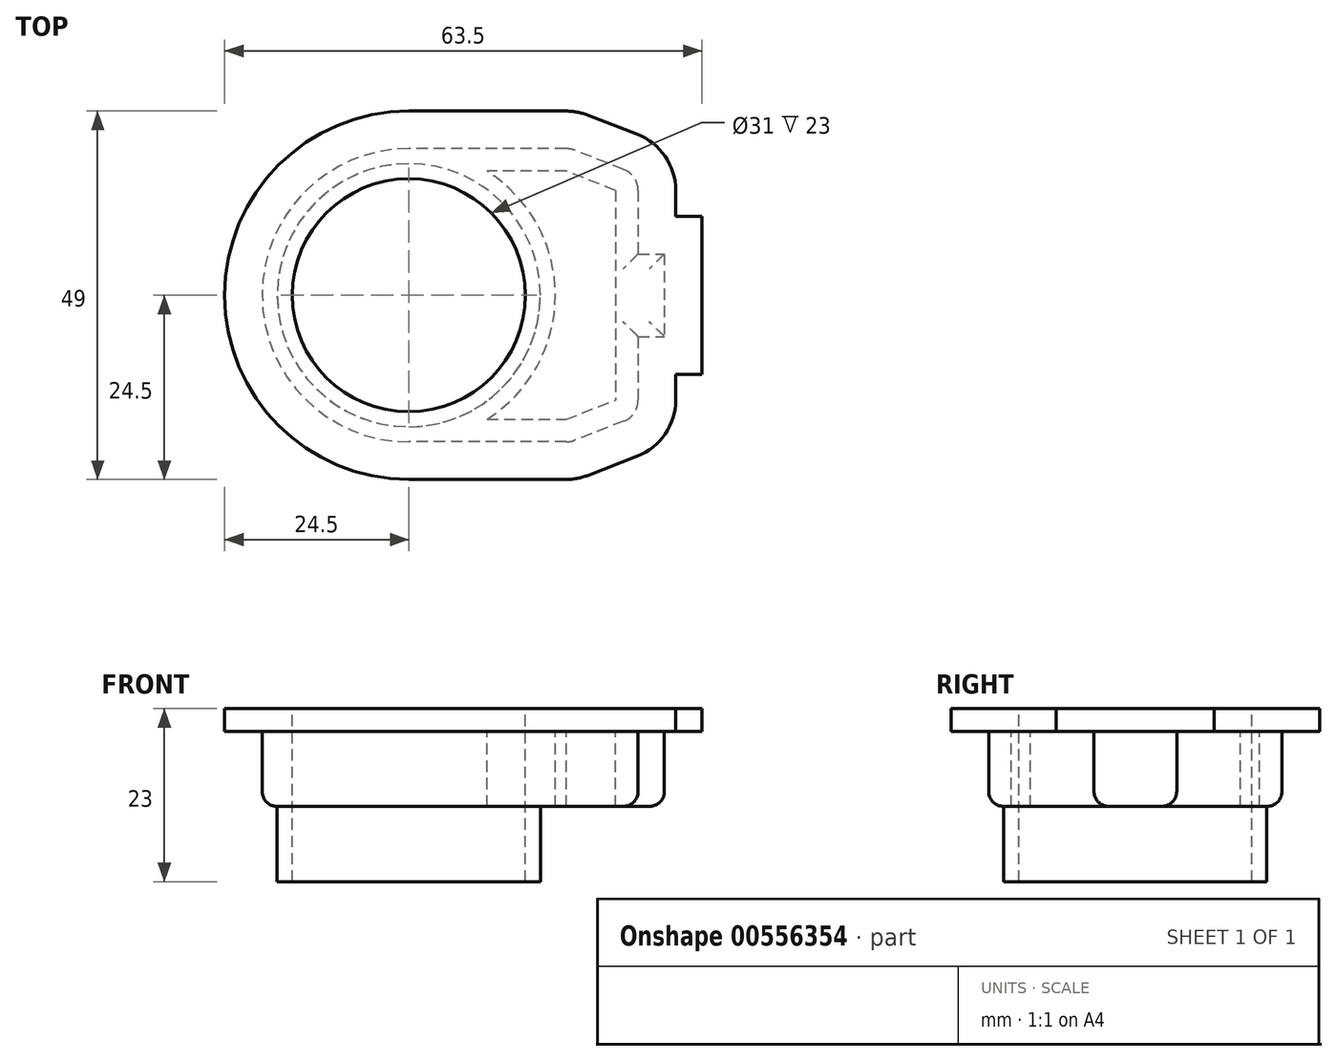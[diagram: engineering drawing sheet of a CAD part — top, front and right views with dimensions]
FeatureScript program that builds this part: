
annotation { "Feature Type Name" : "Feature", "Feature Type Description" : "" }
export const myFeature = defineFeature(function(context is Context, id is Id, definition is map)
    precondition{}
    {
        {
            var Q0;
            Q0=qCreatedBy(makeId("Top.planeOp"),FACE);
            var sketch = newSketch(context, id + "F0", { "sketchPlane" : qUnion([Q0])});
            skCircle(sketch, "E0", {"center": v(0, 0) * mm, "radius": 19.5 * mm});
            skLineSegment(sketch, "E1", {"start": v(30.5, 16) * mm, "end": v(30.5, -16) * mm});
            skLineSegment(sketch, "E2", {"start": v(21.5, 19.5) * mm, "end": v(21.5, -19.5) * mm});
            skPoint(sketch, "E3", {"position": v(21.5, 0) * mm});
            skLineSegment(sketch, "E4", {"start": v(-33.47, 0) * mm, "end": v(41.49, 0) * mm, "construction": true});
            skLineSegment(sketch, "E5", {"start": v(21.5, 19.5) * mm, "end": v(0, 19.5) * mm});
            skLineSegment(sketch, "E6", {"start": v(21.5, -19.5) * mm, "end": v(0, -19.5) * mm});
            skPoint(sketch, "E7", {"position": v(30.5, 0) * mm});
            skLineSegment(sketch, "E8", {"start": v(30.5, 16) * mm, "end": v(21.5, 19.5) * mm});
            skLineSegment(sketch, "E9", {"start": v(30.5, -16) * mm, "end": v(21.5, -19.5) * mm});
            skLineSegment(sketch, "E10.bottom", {"start": v(30.5, 5.5) * mm, "end": v(34, 5.5) * mm});
            skLineSegment(sketch, "E10.top", {"start": v(30.5, -5.5) * mm, "end": v(34, -5.5) * mm});
            skLineSegment(sketch, "E10.left", {"start": v(30.5, 5.5) * mm, "end": v(30.5, -5.5) * mm});
            skLineSegment(sketch, "E10.right", {"start": v(34, 5.5) * mm, "end": v(34, -5.5) * mm});
            skSolve(sketch);
        }
        {
            var Q0;
            {var subQ0=sQuery(id+"F0.wireOp",EDGE,"E0");var subQ1=makeQuery(id+"F0.imprint","INTERSECT",VERTEX,{"derivedFrom":[subQ0,sQuery(id+"F0.wireOp",EDGE,"E5")]});Q0=makeQuery(id+"F0.imprint","IMPRINT",FACE,{"disambiguationData":[TD([[makeQuery(id+"F0.imprint","IMPRINT",EDGE,{"disambiguationData":[TD([[subQ1,-1.0]])],"derivedFrom":subQ0}),1.0]])]});}
            var Q1;
            Q1=makeQuery(id+"F0.imprint","IMPRINT",FACE,{"disambiguationData":[TD([[makeQuery(id+"F0.imprint","IMPRINT",EDGE,{"derivedFrom":sQuery(id+"F0.wireOp",EDGE,"E2")}),-1.0]])]});
            var Q2;
            Q2=makeQuery(id+"F0.imprint","IMPRINT",FACE,{"disambiguationData":[TD([[makeQuery(id+"F0.imprint","IMPRINT",EDGE,{"derivedFrom":sQuery(id+"F0.wireOp",EDGE,"E1")}),-1.0]])]});
            var Q3;
            Q3=makeQuery(id+"F0.imprint","IMPRINT",FACE,{"disambiguationData":[TD([[makeQuery(id+"F0.imprint","IMPRINT",EDGE,{"derivedFrom":sQuery(id+"F0.wireOp",EDGE,"E10.bottom")}),-1.0]])]});
            extrude(context, id + "F1", {"entities" : qUnion([Q0, Q1, Q2, Q3]), "depth" : 10 * mm, "offsetDistance" : 25 * mm});
        }
        {
            var Q0;
            Q0=makeQuery(id+"F1.opExtrude","SWEPT_EDGE",EDGE,{"disambiguationData":[OSD([sQuery(id+"F0.wireOp",EDGE,"E1"),sQuery(id+"F0.wireOp",EDGE,"E8")])]});
            var Q1;
            Q1=makeQuery(id+"F1.opExtrude","SWEPT_EDGE",EDGE,{"disambiguationData":[OSD([sQuery(id+"F0.wireOp",EDGE,"E2"),sQuery(id+"F0.wireOp",EDGE,"E5"),sQuery(id+"F0.wireOp",EDGE,"E8")])]});
            var Q2;
            Q2=makeQuery(id+"F1.opExtrude","SWEPT_EDGE",EDGE,{"disambiguationData":[OSD([sQuery(id+"F0.wireOp",EDGE,"E1"),sQuery(id+"F0.wireOp",EDGE,"E9")])]});
            var Q3;
            Q3=makeQuery(id+"F1.opExtrude","SWEPT_EDGE",EDGE,{"disambiguationData":[OSD([sQuery(id+"F0.wireOp",EDGE,"E2"),sQuery(id+"F0.wireOp",EDGE,"E6"),sQuery(id+"F0.wireOp",EDGE,"E9")])]});
            fillet(context, id + "F2", {"entities" : qUnion([Q0, Q1, Q2, Q3]), "radius" : 3 * mm, "tangentPropagation" : true, "allowEdgeOverflow" : false});
        }
        {
            var Q0;
            Q0=makeQuery(id+"F1.opExtrude","CAP_FACE",FACE,{"disambiguationData":[OSD([sQuery(id+"F0.wireOp",EDGE,"E0"),sQuery(id+"F0.wireOp",EDGE,"E1"),sQuery(id+"F0.wireOp",EDGE,"E5"),sQuery(id+"F0.wireOp",EDGE,"E6"),sQuery(id+"F0.wireOp",EDGE,"E8"),sQuery(id+"F0.wireOp",EDGE,"E9"),sQuery(id+"F0.wireOp",EDGE,"E10.bottom"),sQuery(id+"F0.wireOp",EDGE,"E10.top"),sQuery(id+"F0.wireOp",EDGE,"E10.right")])],"isStart":false});
            var sketch = newSketch(context, id + "F3", { "sketchPlane" : qUnion([Q0])});
            skArc(sketch, "E11.0", {"start": v(0, 16.5) * mm, "mid": v(-16.5, 0) * mm, "end": v(0, -16.5) * mm});
            skLineSegment(sketch, "E11.1", {"start": v(20.94, 16.5) * mm, "end": v(0, 16.5) * mm});
            skLineSegment(sketch, "E11.2", {"start": v(0, -16.5) * mm, "end": v(20.94, -16.5) * mm});
            skLineSegment(sketch, "E11.3", {"start": v(27.5, 13.95) * mm, "end": v(20.94, 16.5) * mm});
            skLineSegment(sketch, "E11.4", {"start": v(27.5, 2.5) * mm, "end": v(27.5, 13.95) * mm});
            skLineSegment(sketch, "E11.5", {"start": v(31, 2.5) * mm, "end": v(27.5, 2.5) * mm});
            skLineSegment(sketch, "E11.6", {"start": v(20.94, -16.5) * mm, "end": v(27.5, -13.95) * mm});
            skLineSegment(sketch, "E11.7", {"start": v(27.5, -13.95) * mm, "end": v(27.5, -2.5) * mm});
            skLineSegment(sketch, "E11.8", {"start": v(27.5, -2.5) * mm, "end": v(31, -2.5) * mm});
            skLineSegment(sketch, "E11.9", {"start": v(31, -2.5) * mm, "end": v(31, 2.5) * mm});
            skLineSegment(sketch, "E12", {"start": v(27.5, 2.5) * mm, "end": v(27.5, -2.5) * mm});
            skArc(sketch, "E13.0", {"start": v(0, 24.5) * mm, "mid": v(-24.5, 0) * mm, "end": v(0, -24.5) * mm});
            skLineSegment(sketch, "E13.1", {"start": v(20.94, 24.5) * mm, "end": v(0, 24.5) * mm});
            skArc(sketch, "E13.2", {"start": v(23.84, 23.96) * mm, "mid": v(22.41, 24.36) * mm, "end": v(20.94, 24.5) * mm});
            skLineSegment(sketch, "E13.3", {"start": v(35.5, -13.95) * mm, "end": v(35.5, -10.5) * mm});
            skArc(sketch, "E13.4", {"start": v(30.4, -21.4) * mm, "mid": v(34.1, -18.46) * mm, "end": v(35.5, -13.95) * mm});
            skLineSegment(sketch, "E13.5", {"start": v(23.84, -23.96) * mm, "end": v(30.4, -21.4) * mm});
            skArc(sketch, "E13.6", {"start": v(20.94, -24.5) * mm, "mid": v(22.41, -24.36) * mm, "end": v(23.84, -23.96) * mm});
            skLineSegment(sketch, "E13.7", {"start": v(35.5, -10.5) * mm, "end": v(39, -10.5) * mm});
            skLineSegment(sketch, "E13.8", {"start": v(39, -10.5) * mm, "end": v(39, 10.5) * mm});
            skLineSegment(sketch, "E13.9", {"start": v(39, 10.5) * mm, "end": v(35.5, 10.5) * mm});
            skLineSegment(sketch, "E13.10", {"start": v(0, -24.5) * mm, "end": v(20.94, -24.5) * mm});
            skLineSegment(sketch, "E13.11", {"start": v(35.5, 10.5) * mm, "end": v(35.5, 13.95) * mm});
            skArc(sketch, "E13.12", {"start": v(35.5, 13.95) * mm, "mid": v(34.1, 18.46) * mm, "end": v(30.4, 21.4) * mm});
            skLineSegment(sketch, "E13.13", {"start": v(30.4, 21.4) * mm, "end": v(23.84, 23.96) * mm});
            skCircle(sketch, "E14", {"center": v(0, 0) * mm, "radius": 16.5 * mm});
            skCircle(sketch, "E15", {"center": v(0, 0) * mm, "radius": 15.5 * mm});
            skCircle(sketch, "E16", {"center": v(0, 0) * mm, "radius": 19.5 * mm});
            skSolve(sketch);
        }
        {
            var Q0;
            Q0=makeQuery(id+"F3.imprint","IMPRINT",FACE,{"disambiguationData":[TD([[makeQuery(id+"F3.imprint","IMPRINT",EDGE,{"derivedFrom":sQuery(id+"F3.wireOp",EDGE,"E15")}),1.0]])]});
            var Q1;
            {var subQ0=sQuery(id+"F3.wireOp",EDGE,"E11.3");Q1=makeQuery(id+"F3.imprint","IMPRINT",FACE,{"disambiguationData":[TD([[makeQuery(id+"F3.imprint","IMPRINT",EDGE,{"derivedFrom":subQ0}),1.0]])]});}
            extrude(context, id + "F4", {"entities" : qUnion([Q0, Q1]), "operationType" : NewBodyOperationType.REMOVE, "oppositeDirection" : true, "depth" : 25 * mm, "offsetDistance" : 25 * mm});
        }
        {
            var Q0;
            Q0=makeQuery(id+"F3.imprint","IMPRINT",FACE,{"disambiguationData":[TD([[makeQuery(id+"F3.imprint","IMPRINT",EDGE,{"derivedFrom":sQuery(id+"F3.wireOp",EDGE,"E13.0")}),1.0]])]});
            var Q1;
            Q1=makeQuery(id+"F3.imprint","IMPRINT",FACE,{"disambiguationData":[TD([[makeQuery(id+"F3.imprint","IMPRINT",EDGE,{"derivedFrom":sQuery(id+"F3.wireOp",EDGE,"E11.0")}),-1.0]])]});
            var Q2;
            Q2=makeQuery(id+"F3.imprint","IMPRINT",FACE,{"disambiguationData":[TD([[makeQuery(id+"F3.imprint","IMPRINT",EDGE,{"derivedFrom":sQuery(id+"F3.wireOp",EDGE,"E11.5")}),1.0]])]});
            var Q3;
            {var subQ13=sQuery(id+"F3.wireOp",EDGE,"E11.1");Q3=makeQuery(id+"F3.imprint","IMPRINT",FACE,{"disambiguationData":[TD([[makeQuery(id+"F3.imprint","IMPRINT",EDGE,{"derivedFrom":subQ13}),-1.0]])]});}
            var Q4;
            {var subQ1=sQuery(id+"F3.wireOp",EDGE,"E11.1");Q4=makeQuery(id+"F3.imprint","IMPRINT",FACE,{"disambiguationData":[TD([[makeQuery(id+"F3.imprint","IMPRINT",EDGE,{"derivedFrom":subQ1}),1.0]])]});}
            var Q5;
            Q5=makeQuery(id+"F3.imprint","IMPRINT",FACE,{"disambiguationData":[TD([[makeQuery(id+"F3.imprint","IMPRINT",EDGE,{"derivedFrom":sQuery(id+"F3.wireOp",EDGE,"E15")}),-1.0]])]});
            var Q6;
            {var subQ13=sQuery(id+"F3.wireOp",EDGE,"E11.3");Q6=makeQuery(id+"F3.imprint","IMPRINT",FACE,{"disambiguationData":[TD([[makeQuery(id+"F3.imprint","IMPRINT",EDGE,{"derivedFrom":subQ13}),-1.0]])]});}
            var Q7;
            {var subQ0=sQuery(id+"F3.wireOp",EDGE,"E11.3");Q7=makeQuery(id+"F3.imprint","IMPRINT",FACE,{"disambiguationData":[TD([[makeQuery(id+"F3.imprint","IMPRINT",EDGE,{"derivedFrom":subQ0}),1.0]])]});}
            extrude(context, id + "F5", {"entities" : qUnion([Q0, Q1, Q2, Q3, Q4, Q5, Q6, Q7]), "operationType" : NewBodyOperationType.ADD, "depth" : 3 * mm, "offsetDistance" : 25 * mm});
        }
        {
            var Q0;
            Q0=makeQuery(id+"F1.opExtrude","CAP_EDGE",EDGE,{"disambiguationData":[OSD([sQuery(id+"F0.wireOp",EDGE,"E0")])],"isStart":true});
            var Q1;
            Q1=makeQuery(id+"F1.opExtrude","CAP_EDGE",EDGE,{"disambiguationData":[OSD([sQuery(id+"F0.wireOp",EDGE,"E6")])],"isStart":true});
            var Q2;
            Q2=makeQuery(id+"F1.opExtrude","CAP_EDGE",EDGE,{"disambiguationData":[OSD([sQuery(id+"F0.wireOp",EDGE,"E9")])],"isStart":true});
            var Q3;
            {var subQ0=sQuery(id+"F0.wireOp",EDGE,"E1");Q3=makeQuery(id+"F1.opExtrude","CAP_EDGE",EDGE,{"disambiguationData":[OSD([subQ0]),TDD([makeQuery(id+"F0.imprint","IMPRINT",EDGE,{"disambiguationData":[TD([[makeQuery(id+"F0.imprint","INTERSECT",VERTEX,{"derivedFrom":[subQ0,sQuery(id+"F0.wireOp",EDGE,"E9")]}),1.0]])],"derivedFrom":subQ0})])],"isStart":true});}
            var Q4;
            {var subQ0=sQuery(id+"F0.wireOp",EDGE,"E9");var subQ1=sQuery(id+"F0.wireOp",EDGE,"E1");Q4=makeQuery(id+"F2.opFillet","BLEND_EDGE",EDGE,{"blendedFrom":[makeQuery(id+"F1.opExtrude","SWEPT_EDGE",EDGE,{"disambiguationData":[OSD([subQ1,subQ0])]}),makeQuery(id+"F1.opExtrude","CAP_FACE",FACE,{"disambiguationData":[OSD([sQuery(id+"F0.wireOp",EDGE,"E0"),subQ1,sQuery(id+"F0.wireOp",EDGE,"E5"),sQuery(id+"F0.wireOp",EDGE,"E6"),sQuery(id+"F0.wireOp",EDGE,"E8"),subQ0,sQuery(id+"F0.wireOp",EDGE,"E10.bottom"),sQuery(id+"F0.wireOp",EDGE,"E10.top"),sQuery(id+"F0.wireOp",EDGE,"E10.right")])],"isStart":true})],"blendedInto":[makeQuery(id+"F1.opExtrude","CAP_FACE",FACE,{"disambiguationData":[OSD([sQuery(id+"F0.wireOp",EDGE,"E0"),subQ1,sQuery(id+"F0.wireOp",EDGE,"E5"),sQuery(id+"F0.wireOp",EDGE,"E6"),sQuery(id+"F0.wireOp",EDGE,"E8"),subQ0,sQuery(id+"F0.wireOp",EDGE,"E10.bottom"),sQuery(id+"F0.wireOp",EDGE,"E10.top"),sQuery(id+"F0.wireOp",EDGE,"E10.right")])],"isStart":true})]});}
            var Q5;
            Q5=makeQuery(id+"F1.opExtrude","CAP_EDGE",EDGE,{"disambiguationData":[OSD([sQuery(id+"F0.wireOp",EDGE,"E10.right")])],"isStart":true});
            var Q6;
            Q6=makeQuery(id+"F1.opExtrude","CAP_EDGE",EDGE,{"disambiguationData":[OSD([sQuery(id+"F0.wireOp",EDGE,"E10.bottom")])],"isStart":true});
            var Q7;
            {var subQ0=sQuery(id+"F0.wireOp",EDGE,"E1");Q7=makeQuery(id+"F1.opExtrude","CAP_EDGE",EDGE,{"disambiguationData":[OSD([subQ0]),TDD([makeQuery(id+"F0.imprint","IMPRINT",EDGE,{"disambiguationData":[TD([[makeQuery(id+"F0.imprint","INTERSECT",VERTEX,{"derivedFrom":[subQ0,sQuery(id+"F0.wireOp",EDGE,"E8")]}),-1.0]])],"derivedFrom":subQ0})])],"isStart":true});}
            var Q8;
            {var subQ0=sQuery(id+"F0.wireOp",EDGE,"E9");var subQ1=sQuery(id+"F0.wireOp",EDGE,"E6");Q8=makeQuery(id+"F2.opFillet","BLEND_EDGE",EDGE,{"blendedFrom":[makeQuery(id+"F1.opExtrude","SWEPT_EDGE",EDGE,{"disambiguationData":[OSD([sQuery(id+"F0.wireOp",EDGE,"E2"),subQ1,subQ0])]}),makeQuery(id+"F1.opExtrude","CAP_FACE",FACE,{"disambiguationData":[OSD([sQuery(id+"F0.wireOp",EDGE,"E0"),sQuery(id+"F0.wireOp",EDGE,"E1"),sQuery(id+"F0.wireOp",EDGE,"E5"),subQ1,sQuery(id+"F0.wireOp",EDGE,"E8"),subQ0,sQuery(id+"F0.wireOp",EDGE,"E10.bottom"),sQuery(id+"F0.wireOp",EDGE,"E10.top"),sQuery(id+"F0.wireOp",EDGE,"E10.right")])],"isStart":true})],"blendedInto":[makeQuery(id+"F1.opExtrude","CAP_FACE",FACE,{"disambiguationData":[OSD([sQuery(id+"F0.wireOp",EDGE,"E0"),sQuery(id+"F0.wireOp",EDGE,"E1"),sQuery(id+"F0.wireOp",EDGE,"E5"),subQ1,sQuery(id+"F0.wireOp",EDGE,"E8"),subQ0,sQuery(id+"F0.wireOp",EDGE,"E10.bottom"),sQuery(id+"F0.wireOp",EDGE,"E10.top"),sQuery(id+"F0.wireOp",EDGE,"E10.right")])],"isStart":true})]});}
            var Q9;
            Q9=makeQuery(id+"F1.opExtrude","CAP_EDGE",EDGE,{"disambiguationData":[OSD([sQuery(id+"F0.wireOp",EDGE,"E5")])],"isStart":true});
            var Q10;
            Q10=makeQuery(id+"F1.opExtrude","CAP_EDGE",EDGE,{"disambiguationData":[OSD([sQuery(id+"F0.wireOp",EDGE,"E8")])],"isStart":true});
            var Q11;
            {var subQ0=sQuery(id+"F0.wireOp",EDGE,"E8");var subQ1=sQuery(id+"F0.wireOp",EDGE,"E1");Q11=makeQuery(id+"F2.opFillet","BLEND_EDGE",EDGE,{"blendedFrom":[makeQuery(id+"F1.opExtrude","SWEPT_EDGE",EDGE,{"disambiguationData":[OSD([subQ1,subQ0])]}),makeQuery(id+"F1.opExtrude","CAP_FACE",FACE,{"disambiguationData":[OSD([sQuery(id+"F0.wireOp",EDGE,"E0"),subQ1,sQuery(id+"F0.wireOp",EDGE,"E5"),sQuery(id+"F0.wireOp",EDGE,"E6"),subQ0,sQuery(id+"F0.wireOp",EDGE,"E9"),sQuery(id+"F0.wireOp",EDGE,"E10.bottom"),sQuery(id+"F0.wireOp",EDGE,"E10.top"),sQuery(id+"F0.wireOp",EDGE,"E10.right")])],"isStart":true})],"blendedInto":[makeQuery(id+"F1.opExtrude","CAP_FACE",FACE,{"disambiguationData":[OSD([sQuery(id+"F0.wireOp",EDGE,"E0"),subQ1,sQuery(id+"F0.wireOp",EDGE,"E5"),sQuery(id+"F0.wireOp",EDGE,"E6"),subQ0,sQuery(id+"F0.wireOp",EDGE,"E9"),sQuery(id+"F0.wireOp",EDGE,"E10.bottom"),sQuery(id+"F0.wireOp",EDGE,"E10.top"),sQuery(id+"F0.wireOp",EDGE,"E10.right")])],"isStart":true})]});}
            var Q12;
            {var subQ0=sQuery(id+"F0.wireOp",EDGE,"E8");var subQ1=sQuery(id+"F0.wireOp",EDGE,"E5");Q12=makeQuery(id+"F2.opFillet","BLEND_EDGE",EDGE,{"blendedFrom":[makeQuery(id+"F1.opExtrude","SWEPT_EDGE",EDGE,{"disambiguationData":[OSD([sQuery(id+"F0.wireOp",EDGE,"E2"),subQ1,subQ0])]}),makeQuery(id+"F1.opExtrude","CAP_FACE",FACE,{"disambiguationData":[OSD([sQuery(id+"F0.wireOp",EDGE,"E0"),sQuery(id+"F0.wireOp",EDGE,"E1"),subQ1,sQuery(id+"F0.wireOp",EDGE,"E6"),subQ0,sQuery(id+"F0.wireOp",EDGE,"E9"),sQuery(id+"F0.wireOp",EDGE,"E10.bottom"),sQuery(id+"F0.wireOp",EDGE,"E10.top"),sQuery(id+"F0.wireOp",EDGE,"E10.right")])],"isStart":true})],"blendedInto":[makeQuery(id+"F1.opExtrude","CAP_FACE",FACE,{"disambiguationData":[OSD([sQuery(id+"F0.wireOp",EDGE,"E0"),sQuery(id+"F0.wireOp",EDGE,"E1"),subQ1,sQuery(id+"F0.wireOp",EDGE,"E6"),subQ0,sQuery(id+"F0.wireOp",EDGE,"E9"),sQuery(id+"F0.wireOp",EDGE,"E10.bottom"),sQuery(id+"F0.wireOp",EDGE,"E10.top"),sQuery(id+"F0.wireOp",EDGE,"E10.right")])],"isStart":true})]});}
            var Q13;
            Q13=makeQuery(id+"F1.opExtrude","CAP_EDGE",EDGE,{"disambiguationData":[OSD([sQuery(id+"F0.wireOp",EDGE,"E10.top")])],"isStart":true});
            fillet(context, id + "F6", {"entities" : qUnion([Q0, Q1, Q2, Q3, Q4, Q5, Q6, Q7, Q8, Q9, Q10, Q11, Q12, Q13]), "radius" : 2 * mm, "tangentPropagation" : true, "allowEdgeOverflow" : false});
        }
        {
            var Q0;
            Q0=makeQuery(id+"F1.opExtrude","CAP_FACE",FACE,{"disambiguationData":[OSD([sQuery(id+"F0.wireOp",EDGE,"E0"),sQuery(id+"F0.wireOp",EDGE,"E1"),sQuery(id+"F0.wireOp",EDGE,"E5"),sQuery(id+"F0.wireOp",EDGE,"E6"),sQuery(id+"F0.wireOp",EDGE,"E8"),sQuery(id+"F0.wireOp",EDGE,"E9"),sQuery(id+"F0.wireOp",EDGE,"E10.bottom"),sQuery(id+"F0.wireOp",EDGE,"E10.top"),sQuery(id+"F0.wireOp",EDGE,"E10.right")])],"isStart":true});
            var sketch = newSketch(context, id + "F7", { "sketchPlane" : qUnion([Q0])});
            skCircle(sketch, "E17", {"center": v(0, 0) * mm, "radius": 15.5 * mm});
            skCircle(sketch, "E18", {"center": v(0, 0) * mm, "radius": 17.5 * mm});
            skSolve(sketch);
        }
        {
            var Q0;
            Q0=makeQuery(id+"F7.imprint","IMPRINT",FACE,{"disambiguationData":[TD([[makeQuery(id+"F7.imprint","IMPRINT",EDGE,{"derivedFrom":sQuery(id+"F7.wireOp",EDGE,"E17")}),1.0]])]});
            extrude(context, id + "F8", {"entities" : qUnion([Q0]), "operationType" : NewBodyOperationType.ADD, "depth" : 10 * mm, "offsetDistance" : 25 * mm});
        }
    });
